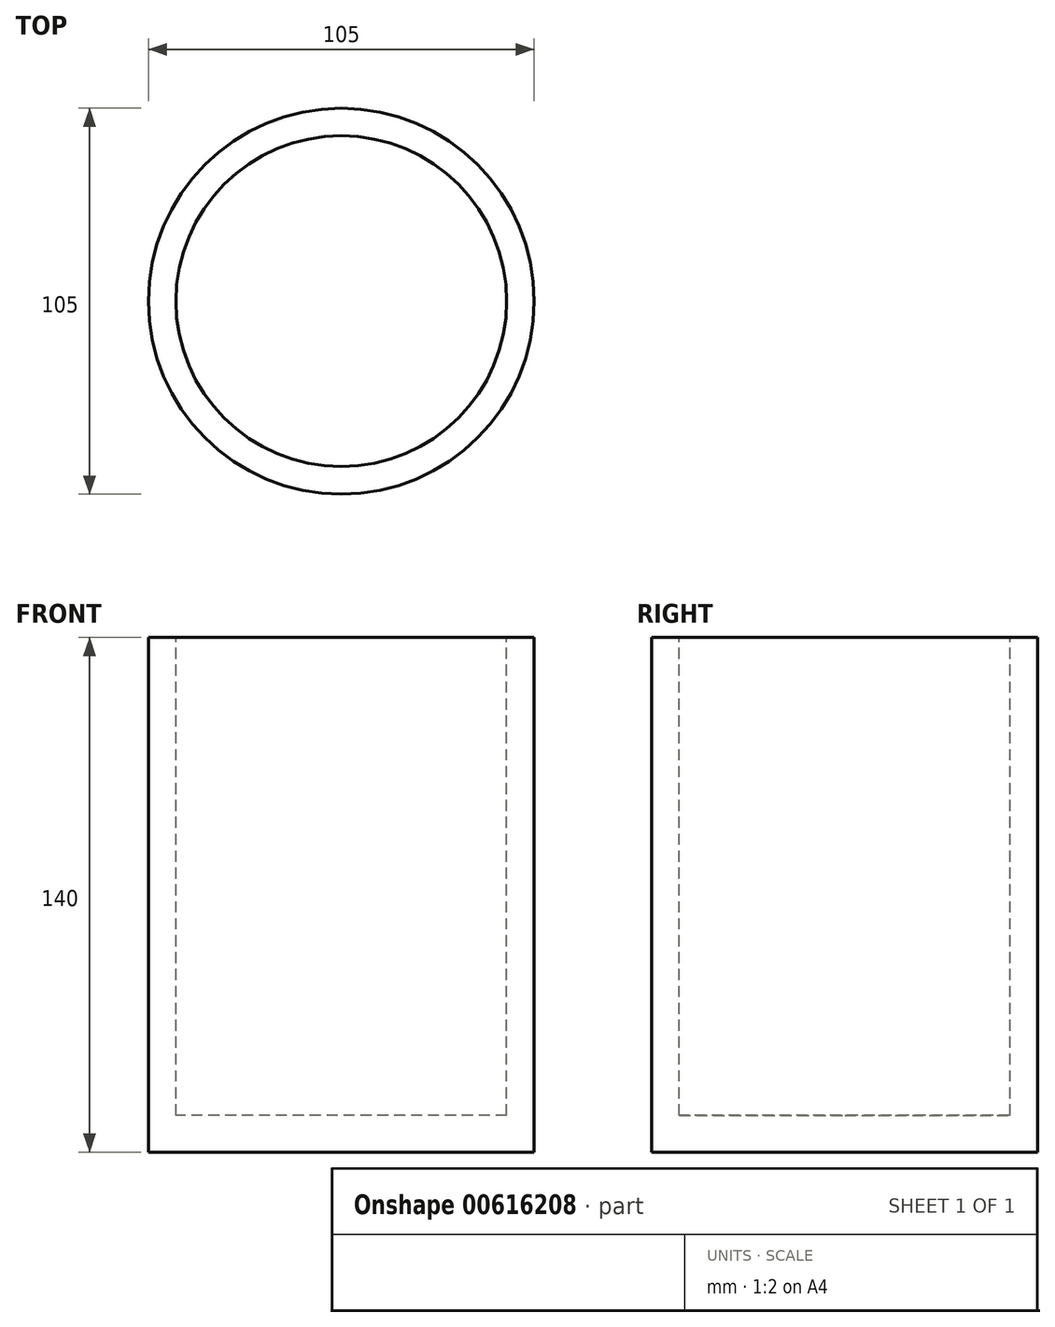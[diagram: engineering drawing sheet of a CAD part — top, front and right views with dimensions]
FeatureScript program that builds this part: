
annotation { "Feature Type Name" : "Feature", "Feature Type Description" : "" }
export const myFeature = defineFeature(function(context is Context, id is Id, definition is map)
    precondition{}
    {
        {
            var Q0;
            Q0=qCreatedBy(makeId("Top.planeOp"),FACE);
            var sketch = newSketch(context, id + "F0", { "sketchPlane" : qUnion([Q0])});
            skCircle(sketch, "E0", {"center": v(0, 0) * mm, "radius": 52.5 * mm});
            skSolve(sketch);
        }
        {
            var Q0;
            Q0=makeQuery(id+"F0.imprint","IMPRINT",FACE,{"disambiguationData":[TD([[makeQuery(id+"F0.imprint","IMPRINT",EDGE,{"derivedFrom":sQuery(id+"F0.wireOp",EDGE,"E0")}),1.0]])]});
            extrude(context, id + "F1", {"entities" : qUnion([Q0]), "depth" : 140 * mm, "offsetDistance" : 25 * mm});
        }
        {
            var Q0;
            Q0=qCreatedBy(makeId("Front.planeOp"),FACE);
            var sketch = newSketch(context, id + "F2", { "sketchPlane" : qUnion([Q0])});
            skFitSpline(sketch, "E1", {"points": [v(46.7, 119.1) * mm, v(81.68, 113.96) * mm, v(90.1, 65) * mm, v(78.18, 33.63) * mm, v(46.26, 18.05) * mm], "startDerivative": vector(202.88, 16) * mm, "endDerivative": vector(-285.66, -9.37) * mm});
            skSolve(sketch);
        }
        {
            var Q0;
            Q0=qCreatedBy(makeId("Right.planeOp"),FACE);
            var Q1;
            Q1 = qBodyType(qCreatedBy(id + "F4" ,EDGE), BodyType.WIRE);
            cPlane(context, id + "F3", {"entities" : qUnion([Q0, Q1]), "cplaneType" : CPlaneType.OFFSET, "offset" : 48 * mm, "width" : 150 * mm, "height" : 150 * mm});
        }
        {
            var Q0;
            Q0=qCreatedBy(id+"F3.planeOp",FACE);
            var sketch = newSketch(context, id + "F4", { "sketchPlane" : qUnion([Q0])});
            skCircle(sketch, "E2", {"center": v(0, 118.82) * mm, "radius": 5 * mm});
            skSolve(sketch);
        }
        {
            var Q0;
            Q0=makeQuery(id+"F1.opExtrude","CAP_FACE",FACE,{"disambiguationData":[OSD([sQuery(id+"F0.wireOp",EDGE,"E0")])],"isStart":false});
            var sketch = newSketch(context, id + "F5", { "sketchPlane" : qUnion([Q0])});
            skCircle(sketch, "E3", {"center": v(0, 0) * mm, "radius": 45 * mm});
            skSolve(sketch);
        }
        {
            var Q0;
            Q0=makeQuery(id+"F5.imprint","IMPRINT",FACE,{"disambiguationData":[TD([[makeQuery(id+"F5.imprint","IMPRINT",EDGE,{"derivedFrom":sQuery(id+"F5.wireOp",EDGE,"E3")}),1.0]])]});
            extrude(context, id + "F6", {"entities" : qUnion([Q0]), "operationType" : NewBodyOperationType.REMOVE, "oppositeDirection" : true, "depth" : 130 * mm, "offsetDistance" : 25 * mm});
        }
    });
